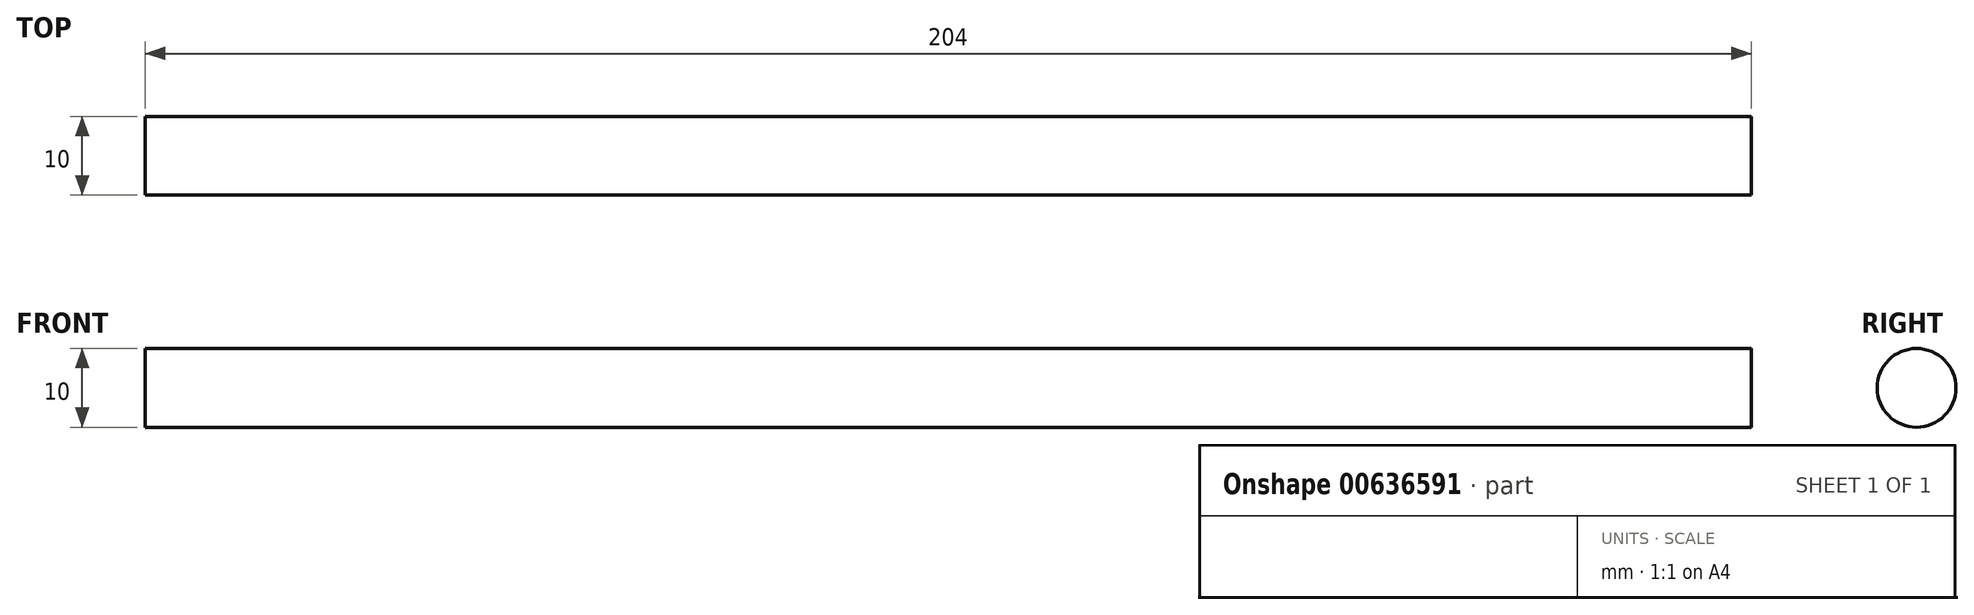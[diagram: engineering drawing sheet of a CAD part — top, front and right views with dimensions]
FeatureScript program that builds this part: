
annotation { "Feature Type Name" : "Feature", "Feature Type Description" : "" }
export const myFeature = defineFeature(function(context is Context, id is Id, definition is map)
    precondition{}
    {
        {
            var Q0;
            Q0=qCreatedBy(makeId("Right.planeOp"),FACE);
            var sketch = newSketch(context, id + "F0", { "sketchPlane" : qUnion([Q0])});
            skCircle(sketch, "E0", {"center": v(0, 0) * mm, "radius": 5 * mm});
            skSolve(sketch);
        }
        {
            var Q0;
            Q0 = qSketchRegion(id + "F0", true);
            extrude(context, id + "F1", {"entities" : qUnion([Q0]), "depth" : 204 * mm, "offsetDistance" : 25 * mm});
        }
    });
